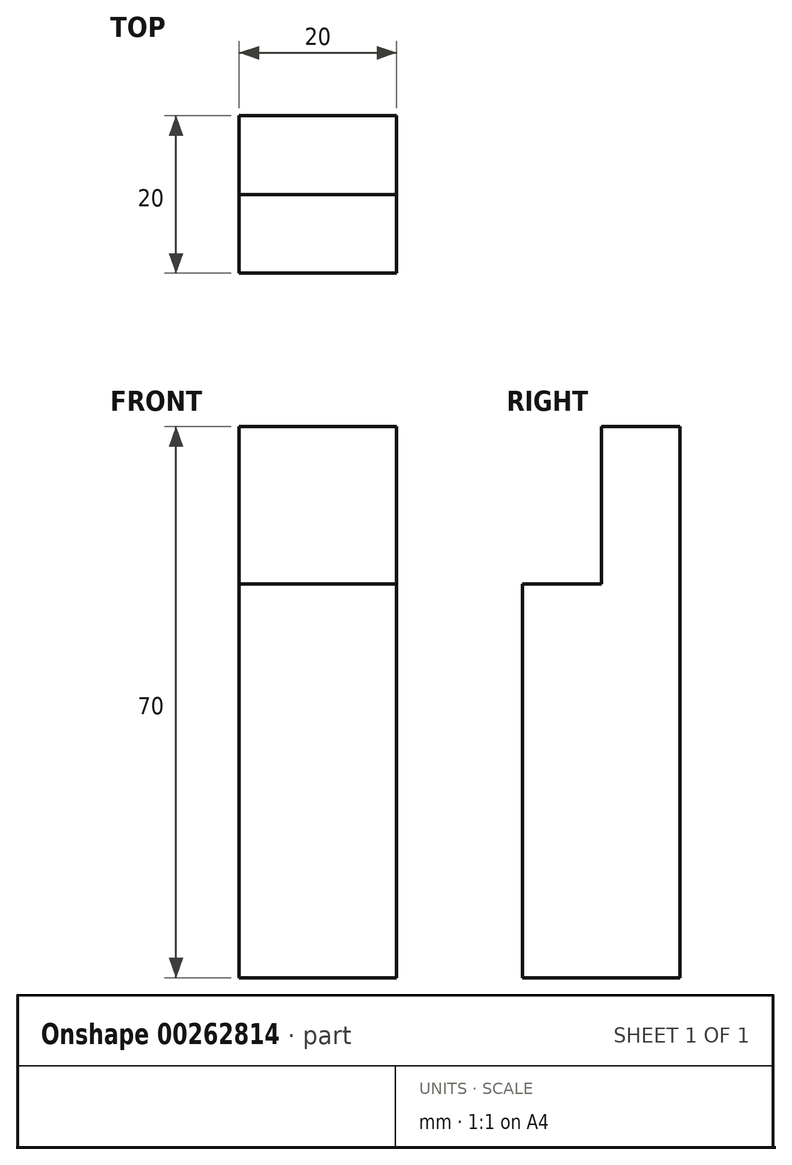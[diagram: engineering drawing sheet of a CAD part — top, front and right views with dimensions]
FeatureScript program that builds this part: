
annotation { "Feature Type Name" : "Feature", "Feature Type Description" : "" }
export const myFeature = defineFeature(function(context is Context, id is Id, definition is map)
    precondition{}
    {
        {
            var Q0;
            Q0=qCreatedBy(makeId("Front.planeOp"),FACE);
            var sketch = newSketch(context, id + "F0", { "sketchPlane" : qUnion([Q0])});
            skLineSegment(sketch, "E0.bottom", {"start": v(-14.36, 44.71) * mm, "end": v(5.64, 44.71) * mm});
            skLineSegment(sketch, "E0.top", {"start": v(-14.36, -25.29) * mm, "end": v(5.64, -25.29) * mm});
            skLineSegment(sketch, "E0.left", {"start": v(-14.36, 44.71) * mm, "end": v(-14.36, -25.29) * mm});
            skLineSegment(sketch, "E0.right", {"start": v(5.64, 44.71) * mm, "end": v(5.64, -25.29) * mm});
            skLineSegment(sketch, "E1", {"start": v(-14.36, 24.71) * mm, "end": v(5.64, 24.71) * mm});
            skSolve(sketch);
        }
        {
            var Q0;
            Q0=makeQuery(id+"F0.imprint","IMPRINT",FACE,{"disambiguationData":[TD([[makeQuery(id+"F0.imprint","IMPRINT",EDGE,{"derivedFrom":sQuery(id+"F0.wireOp",EDGE,"E0.bottom")}),-1.0]])]});
            var Q1;
            {var subQ0=sQuery(id+"F0.wireOp",EDGE,"E0.top");Q1=makeQuery(id+"F0.imprint","IMPRINT",FACE,{"disambiguationData":[TD([[makeQuery(id+"F0.imprint","IMPRINT",EDGE,{"derivedFrom":subQ0}),1.0]])]});}
            extrude(context, id + "F1", {"entities" : qUnion([Q0, Q1]), "oppositeDirection" : true, "depth" : 20 * mm});
        }
        {
            var Q0;
            {var subQ0=sQuery(id+"F0.wireOp",EDGE,"E0.bottom");Q0=makeQuery(id+"F0.imprint","IMPRINT",FACE,{"disambiguationData":[TD([[makeQuery(id+"F0.imprint","IMPRINT",EDGE,{"derivedFrom":subQ0}),-1.0]])]});}
            extrude(context, id + "F2", {"entities" : qUnion([Q0]), "operationType" : NewBodyOperationType.REMOVE, "oppositeDirection" : true, "depth" : 10 * mm});
        }
    });
